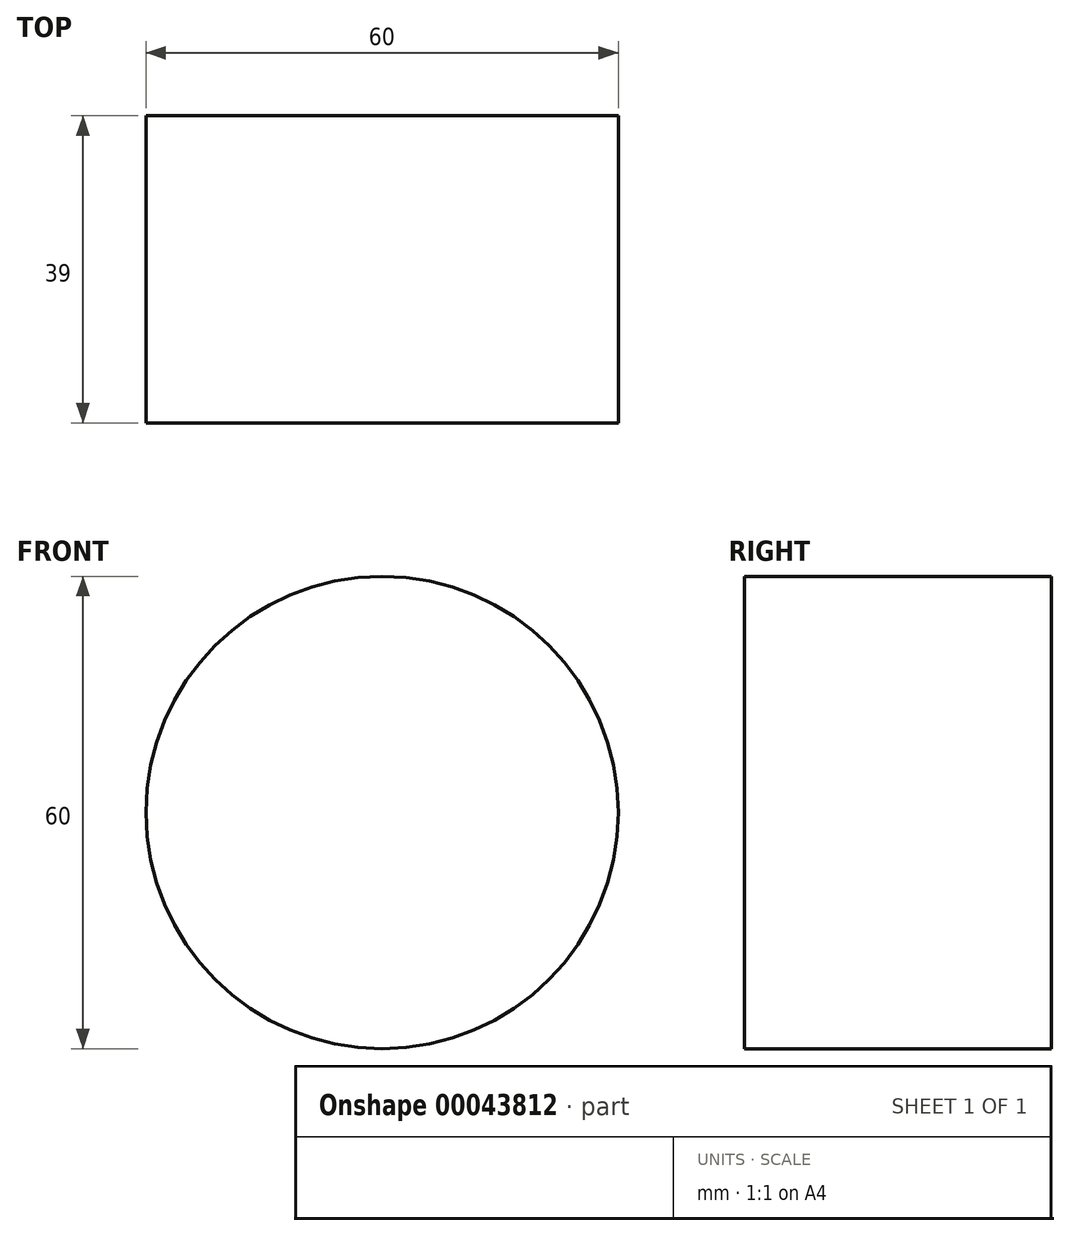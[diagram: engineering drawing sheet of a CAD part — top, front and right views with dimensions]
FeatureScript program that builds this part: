
annotation { "Feature Type Name" : "Feature", "Feature Type Description" : "" }
export const myFeature = defineFeature(function(context is Context, id is Id, definition is map)
    precondition{}
    {
        {
            var Q0;
            Q0=qCreatedBy(makeId("Front.planeOp"),FACE);
            var sketch = newSketch(context, id + "F0", { "sketchPlane" : qUnion([Q0])});
            skCircle(sketch, "E0", {"center": v(0, 0) * mm, "radius": 30 * mm});
            skSolve(sketch);
        }
        {
            var Q0;
            Q0=makeQuery(id+"F0.imprint","IMPRINT",FACE,{"disambiguationData":[TD([[makeQuery(id+"F0.imprint","IMPRINT",EDGE,{"derivedFrom":sQuery(id+"F0.wireOp",EDGE,"E0")}),1.0]])]});
            extrude(context, id + "F1", {"entities" : qUnion([Q0]), "depth" : 39 * mm});
        }
    });
